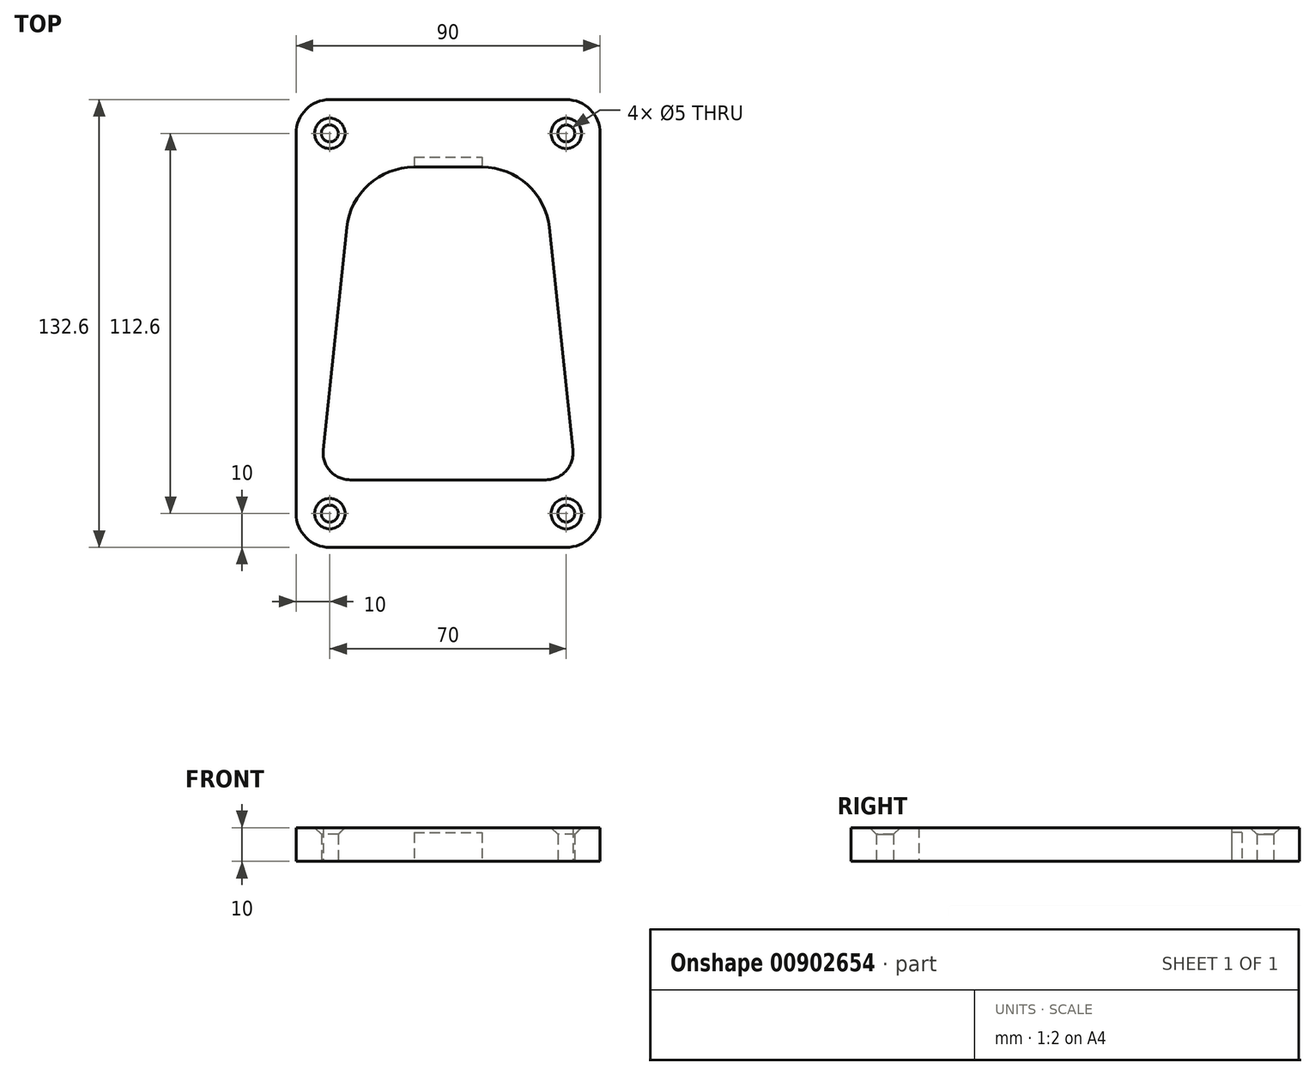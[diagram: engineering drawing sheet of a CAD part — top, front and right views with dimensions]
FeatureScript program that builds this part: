
annotation { "Feature Type Name" : "Feature", "Feature Type Description" : "" }
export const myFeature = defineFeature(function(context is Context, id is Id, definition is map)
    precondition{}
    {
        {
            var Q0;
            Q0=qCreatedBy(makeId("Top.planeOp"),FACE);
            var sketch = newSketch(context, id + "F0", { "sketchPlane" : qUnion([Q0])});
            skLineSegment(sketch, "E0", {"start": v(0, 0) * mm, "end": v(0, 92.6) * mm, "construction": true});
            skLineSegment(sketch, "E1", {"start": v(-10.11, 92.6) * mm, "end": v(10.11, 92.6) * mm});
            skLineSegment(sketch, "E2", {"start": v(-29, 0) * mm, "end": v(29, 0) * mm});
            skArc(sketch, "E3", {"start": v(29, 0) * mm, "mid": v(34.95, 2.65) * mm, "end": v(36.96, 8.84) * mm});
            skArc(sketch, "E4", {"start": v(30, 74.7) * mm, "mid": v(23.49, 87.47) * mm, "end": v(10.11, 92.6) * mm});
            skLineSegment(sketch, "E5", {"start": v(36.96, 8.84) * mm, "end": v(30, 74.7) * mm});
            skArc(sketch, "E6.MirrorCS", {"start": v(-30, 74.7) * mm, "mid": v(-23.49, 87.47) * mm, "end": v(-10.11, 92.6) * mm});
            skLineSegment(sketch, "E7.MirrorCS", {"start": v(-36.96, 8.84) * mm, "end": v(-30, 74.7) * mm});
            skArc(sketch, "E8.MirrorCS", {"start": v(-29, 0) * mm, "mid": v(-34.95, 2.65) * mm, "end": v(-36.96, 8.84) * mm});
            skLineSegment(sketch, "E9", {"start": v(37, 0) * mm, "end": v(37, 88.48) * mm, "construction": true});
            skLineSegment(sketch, "E10.bottom", {"start": v(-35, -20) * mm, "end": v(35, -20) * mm});
            skLineSegment(sketch, "E10.top", {"start": v(-35, 112.6) * mm, "end": v(35, 112.6) * mm});
            skLineSegment(sketch, "E10.left", {"start": v(-45, -10) * mm, "end": v(-45, 102.6) * mm});
            skLineSegment(sketch, "E10.right", {"start": v(45, -10) * mm, "end": v(45, 102.6) * mm});
            skPoint(sketch, "E11.visualSharp", {"position": v(45, -20) * mm});
            skArc(sketch, "E11.filletArc", {"start": v(35, -20) * mm, "mid": v(42.07, -17.07) * mm, "end": v(45, -10) * mm});
            skPoint(sketch, "E12.visualSharp", {"position": v(-45, -20) * mm});
            skArc(sketch, "E12.filletArc", {"start": v(-45, -10) * mm, "mid": v(-42.07, -17.07) * mm, "end": v(-35, -20) * mm});
            skPoint(sketch, "E13.visualSharp", {"position": v(-45, 112.6) * mm});
            skArc(sketch, "E13.filletArc", {"start": v(-35, 112.6) * mm, "mid": v(-42.07, 109.67) * mm, "end": v(-45, 102.6) * mm});
            skPoint(sketch, "E14.visualSharp", {"position": v(45, 112.6) * mm});
            skArc(sketch, "E14.filletArc", {"start": v(45, 102.6) * mm, "mid": v(42.07, 109.67) * mm, "end": v(35, 112.6) * mm});
            skCircle(sketch, "E15", {"center": v(-35, 102.6) * mm, "radius": 2.5 * mm});
            skCircle(sketch, "E16", {"center": v(35, 102.6) * mm, "radius": 2.5 * mm});
            skCircle(sketch, "E17", {"center": v(-35, -10) * mm, "radius": 2.5 * mm});
            skCircle(sketch, "E18", {"center": v(35, -10) * mm, "radius": 2.5 * mm});
            skCircle(sketch, "E19", {"center": v(35, -10) * mm, "radius": 10 * mm, "construction": true});
            skCircle(sketch, "E20", {"center": v(35, 102.6) * mm, "radius": 10 * mm, "construction": true});
            skLineSegment(sketch, "E21", {"start": v(-10, 95.6) * mm, "end": v(10, 95.6) * mm});
            skLineSegment(sketch, "E22", {"start": v(10, 95.6) * mm, "end": v(10, 92.6) * mm});
            skLineSegment(sketch, "E23", {"start": v(-10, 95.6) * mm, "end": v(-10, 92.6) * mm});
            skSolve(sketch);
        }
        {
            var Q0;
            Q0=makeQuery(id+"F0.imprint","IMPRINT",FACE,{"disambiguationData":[TD([[makeQuery(id+"F0.imprint","IMPRINT",EDGE,{"derivedFrom":sQuery(id+"F0.wireOp",EDGE,"E1")}),1.0]])]});
            var Q1;
            Q1=makeQuery(id+"F0.imprint","IMPRINT",FACE,{"disambiguationData":[TD([[makeQuery(id+"F0.imprint","IMPRINT",EDGE,{"derivedFrom":sQuery(id+"F0.wireOp",EDGE,"E21")}),-1.0]])]});
            extrude(context, id + "F1", {"entities" : qUnion([Q0, Q1]), "depth" : 10 * mm, "offsetDistance" : 25 * mm});
        }
        {
            var Q0;
            Q0=makeQuery(id+"F1.opExtrude","CAP_EDGE",EDGE,{"disambiguationData":[OSD([sQuery(id+"F0.wireOp",EDGE,"E17")])],"isStart":false});
            var Q1;
            Q1=makeQuery(id+"F1.opExtrude","CAP_EDGE",EDGE,{"disambiguationData":[OSD([sQuery(id+"F0.wireOp",EDGE,"E18")])],"isStart":false});
            var Q2;
            Q2=makeQuery(id+"F1.opExtrude","CAP_EDGE",EDGE,{"disambiguationData":[OSD([sQuery(id+"F0.wireOp",EDGE,"E16")])],"isStart":false});
            var Q3;
            Q3=makeQuery(id+"F1.opExtrude","CAP_EDGE",EDGE,{"disambiguationData":[OSD([sQuery(id+"F0.wireOp",EDGE,"E15")])],"isStart":false});
            chamfer(context, id + "F2", {"entities" : qUnion([Q0, Q1, Q2, Q3]), "width" : 2 * mm, "tangentPropagation" : true});
        }
        {
            var Q0;
            Q0=makeQuery(id+"F0.imprint","IMPRINT",FACE,{"disambiguationData":[TD([[makeQuery(id+"F0.imprint","IMPRINT",EDGE,{"derivedFrom":sQuery(id+"F0.wireOp",EDGE,"E21")}),-1.0]])]});
            extrude(context, id + "F3", {"entities" : qUnion([Q0]), "operationType" : NewBodyOperationType.REMOVE, "depth" : 8.5 * mm, "offsetDistance" : 25 * mm});
        }
    });
